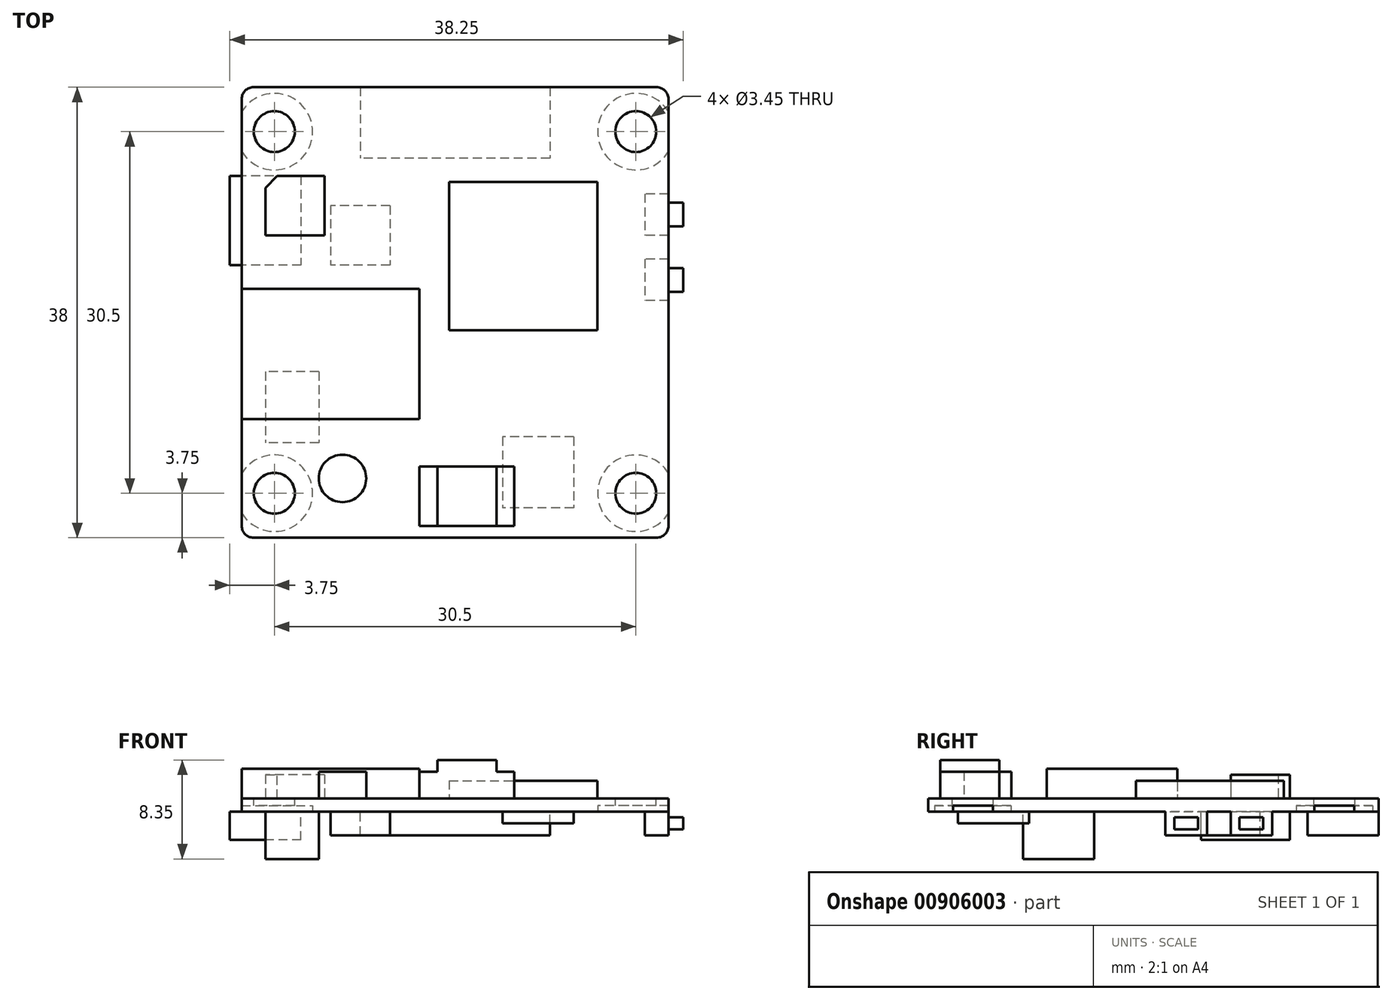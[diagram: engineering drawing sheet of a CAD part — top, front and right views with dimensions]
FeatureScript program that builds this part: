
annotation { "Feature Type Name" : "Feature", "Feature Type Description" : "" }
export const myFeature = defineFeature(function(context is Context, id is Id, definition is map)
    precondition{}
    {
        {
            var Q0;
            Q0=qCreatedBy(makeId("Top.planeOp"),FACE);
            var sketch = newSketch(context, id + "F0", { "sketchPlane" : qUnion([Q0])});
            skLineSegment(sketch, "E0.bottom", {"start": v(17, -19) * mm, "end": v(-17, -19) * mm});
            skLineSegment(sketch, "E0.top", {"start": v(17, 19) * mm, "end": v(-17, 19) * mm});
            skLineSegment(sketch, "E0.left", {"start": v(18, -18) * mm, "end": v(18, 18) * mm});
            skLineSegment(sketch, "E0.right", {"start": v(-18, -18) * mm, "end": v(-18, 18) * mm});
            skPoint(sketch, "E0.middle", {"position": v(0, 0) * mm});
            skPoint(sketch, "E1.visualSharp", {"position": v(-18, 19) * mm});
            skArc(sketch, "E1.filletArc", {"start": v(-17, 19) * mm, "mid": v(-17.7, 18.7) * mm, "end": v(-18, 18) * mm});
            skPoint(sketch, "E2.visualSharp", {"position": v(18, 19) * mm});
            skArc(sketch, "E2.filletArc", {"start": v(18, 18) * mm, "mid": v(17.7, 18.7) * mm, "end": v(17, 19) * mm});
            skPoint(sketch, "E3.visualSharp", {"position": v(-18, -19) * mm});
            skArc(sketch, "E3.filletArc", {"start": v(-18, -18) * mm, "mid": v(-17.7, -18.7) * mm, "end": v(-17, -19) * mm});
            skPoint(sketch, "E4.visualSharp", {"position": v(18, -19) * mm});
            skArc(sketch, "E4.filletArc", {"start": v(17, -19) * mm, "mid": v(17.7, -18.7) * mm, "end": v(18, -18) * mm});
            skSolve(sketch);
        }
        {
            var Q0;
            Q0=qSketchRegion(id+"F0",true);
            extrude(context, id + "F1", {"entities" : qUnion([Q0]), "depth" : 1.1 * mm, "offsetDistance" : 25 * mm});
        }
        {
            var Q0;
            Q0=makeQuery(id+"F1.opExtrude","CAP_FACE",FACE,{"disambiguationData":[OSD([sQuery(id+"F0.wireOp",EDGE,"E0.bottom"),sQuery(id+"F0.wireOp",EDGE,"E0.top"),sQuery(id+"F0.wireOp",EDGE,"E0.left"),sQuery(id+"F0.wireOp",EDGE,"E0.right"),sQuery(id+"F0.wireOp",EDGE,"E1.filletArc"),sQuery(id+"F0.wireOp",EDGE,"E2.filletArc"),sQuery(id+"F0.wireOp",EDGE,"E3.filletArc"),sQuery(id+"F0.wireOp",EDGE,"E4.filletArc")])],"isStart":false});
            var sketch = newSketch(context, id + "F2", { "sketchPlane" : qUnion([Q0])});
            skCircle(sketch, "E5", {"center": v(-15.25, 15.25) * mm, "radius": 1.73 * mm});
            skCircle(sketch, "E6", {"center": v(15.25, 15.25) * mm, "radius": 1.73 * mm});
            skCircle(sketch, "E7", {"center": v(15.25, -15.25) * mm, "radius": 1.73 * mm});
            skCircle(sketch, "E8", {"center": v(-15.25, -15.25) * mm, "radius": 1.73 * mm});
            skSolve(sketch);
        }
        {
            var Q0;
            Q0=qSketchRegion(id+"F2",true);
            extrude(context, id + "F3", {"entities" : qUnion([Q0]), "operationType" : NewBodyOperationType.REMOVE, "endBound" : BoundingType.THROUGH_ALL, "oppositeDirection" : true, "depth" : 25 * mm, "offsetDistance" : 25 * mm});
        }
        {
            var Q0;
            Q0=makeQuery(id+"F1.opExtrude","CAP_FACE",FACE,{"disambiguationData":[OSD([sQuery(id+"F0.wireOp",EDGE,"E0.bottom"),sQuery(id+"F0.wireOp",EDGE,"E0.top"),sQuery(id+"F0.wireOp",EDGE,"E0.left"),sQuery(id+"F0.wireOp",EDGE,"E0.right"),sQuery(id+"F0.wireOp",EDGE,"E1.filletArc"),sQuery(id+"F0.wireOp",EDGE,"E2.filletArc"),sQuery(id+"F0.wireOp",EDGE,"E3.filletArc"),sQuery(id+"F0.wireOp",EDGE,"E4.filletArc")])],"isStart":true});
            var sketch = newSketch(context, id + "F4", { "sketchPlane" : qUnion([Q0])});
            skLineSegment(sketch, "E9.bottom", {"start": v(8, -19) * mm, "end": v(-8, -19) * mm});
            skLineSegment(sketch, "E9.top", {"start": v(8, -13) * mm, "end": v(-8, -13) * mm});
            skLineSegment(sketch, "E9.left", {"start": v(8, -19) * mm, "end": v(8, -13) * mm});
            skLineSegment(sketch, "E9.right", {"start": v(-8, -19) * mm, "end": v(-8, -13) * mm});
            skPoint(sketch, "E10", {"position": v(0, -19) * mm});
            skSolve(sketch);
        }
        {
            var Q0;
            Q0=qSketchRegion(id+"F4",true);
            extrude(context, id + "F5", {"entities" : qUnion([Q0]), "operationType" : NewBodyOperationType.ADD, "depth" : 2 * mm, "offsetDistance" : 25 * mm});
        }
        {
            var Q0;
            Q0=makeQuery(id+"F1.opExtrude","CAP_FACE",FACE,{"disambiguationData":[OSD([sQuery(id+"F0.wireOp",EDGE,"E0.bottom"),sQuery(id+"F0.wireOp",EDGE,"E0.top"),sQuery(id+"F0.wireOp",EDGE,"E0.left"),sQuery(id+"F0.wireOp",EDGE,"E0.right"),sQuery(id+"F0.wireOp",EDGE,"E1.filletArc"),sQuery(id+"F0.wireOp",EDGE,"E2.filletArc"),sQuery(id+"F0.wireOp",EDGE,"E3.filletArc"),sQuery(id+"F0.wireOp",EDGE,"E4.filletArc")])],"isStart":true});
            var sketch = newSketch(context, id + "F6", { "sketchPlane" : qUnion([Q0])});
            skLineSegment(sketch, "E11.bottom", {"start": v(-5.5, -9) * mm, "end": v(-10.5, -9) * mm});
            skLineSegment(sketch, "E11.top", {"start": v(-5.5, -4) * mm, "end": v(-10.5, -4) * mm});
            skLineSegment(sketch, "E11.left", {"start": v(-5.5, -9) * mm, "end": v(-5.5, -4) * mm});
            skLineSegment(sketch, "E11.right", {"start": v(-10.5, -9) * mm, "end": v(-10.5, -4) * mm});
            skPoint(sketch, "E12", {"position": v(-8, -9) * mm});
            skSolve(sketch);
        }
        {
            var Q0;
            Q0=qSketchRegion(id+"F6",true);
            extrude(context, id + "F7", {"entities" : qUnion([Q0]), "operationType" : NewBodyOperationType.ADD, "depth" : 2 * mm, "offsetDistance" : 25 * mm});
        }
        {
            var Q0;
            Q0=makeQuery(id+"F1.opExtrude","CAP_FACE",FACE,{"disambiguationData":[OSD([sQuery(id+"F0.wireOp",EDGE,"E0.bottom"),sQuery(id+"F0.wireOp",EDGE,"E0.top"),sQuery(id+"F0.wireOp",EDGE,"E0.left"),sQuery(id+"F0.wireOp",EDGE,"E0.right"),sQuery(id+"F0.wireOp",EDGE,"E1.filletArc"),sQuery(id+"F0.wireOp",EDGE,"E2.filletArc"),sQuery(id+"F0.wireOp",EDGE,"E3.filletArc"),sQuery(id+"F0.wireOp",EDGE,"E4.filletArc")])],"isStart":true});
            var sketch = newSketch(context, id + "F8", { "sketchPlane" : qUnion([Q0])});
            skLineSegment(sketch, "E13.bottom", {"start": v(-13, -11.5) * mm, "end": v(-19, -11.5) * mm});
            skLineSegment(sketch, "E13.top", {"start": v(-13, -4) * mm, "end": v(-19, -4) * mm});
            skLineSegment(sketch, "E13.left", {"start": v(-13, -11.5) * mm, "end": v(-13, -4) * mm});
            skLineSegment(sketch, "E13.right", {"start": v(-19, -11.5) * mm, "end": v(-19, -4) * mm});
            skSolve(sketch);
        }
        {
            var Q0;
            Q0=qSketchRegion(id+"F8",true);
            extrude(context, id + "F9", {"entities" : qUnion([Q0]), "operationType" : NewBodyOperationType.ADD, "depth" : 2.4 * mm, "offsetDistance" : 25 * mm});
        }
        {
            var Q0;
            Q0=makeQuery(id+"F1.opExtrude","CAP_FACE",FACE,{"disambiguationData":[OSD([sQuery(id+"F0.wireOp",EDGE,"E0.bottom"),sQuery(id+"F0.wireOp",EDGE,"E0.top"),sQuery(id+"F0.wireOp",EDGE,"E0.left"),sQuery(id+"F0.wireOp",EDGE,"E0.right"),sQuery(id+"F0.wireOp",EDGE,"E1.filletArc"),sQuery(id+"F0.wireOp",EDGE,"E2.filletArc"),sQuery(id+"F0.wireOp",EDGE,"E3.filletArc"),sQuery(id+"F0.wireOp",EDGE,"E4.filletArc")])],"isStart":true});
            var sketch = newSketch(context, id + "F10", { "sketchPlane" : qUnion([Q0])});
            skLineSegment(sketch, "E14.bottom", {"start": v(-11.5, 5) * mm, "end": v(-16, 5) * mm});
            skLineSegment(sketch, "E14.top", {"start": v(-11.5, 11) * mm, "end": v(-16, 11) * mm});
            skLineSegment(sketch, "E14.left", {"start": v(-11.5, 5) * mm, "end": v(-11.5, 11) * mm});
            skLineSegment(sketch, "E14.right", {"start": v(-16, 5) * mm, "end": v(-16, 11) * mm});
            skSolve(sketch);
        }
        {
            var Q0;
            Q0=makeQuery(id+"F10.imprint","IMPRINT",FACE,{"disambiguationData":[TD([[makeQuery(id+"F10.imprint","IMPRINT",EDGE,{"derivedFrom":sQuery(id+"F10.wireOp",EDGE,"E14.bottom")}),1.0]])]});
            var sketch = newSketch(context, id + "F11", { "sketchPlane" : qUnion([Q0])});
            skCircle(sketch, "E15.0", {"center": v(15.25, -15.25) * mm, "radius": 1.73 * mm});
            skCircle(sketch, "E16.0", {"center": v(15.25, -15.25) * mm, "radius": 3.23 * mm});
            skCircle(sketch, "E17.0", {"center": v(-15.25, -15.25) * mm, "radius": 3.23 * mm});
            skCircle(sketch, "E18.0", {"center": v(15.25, 15.25) * mm, "radius": 3.23 * mm});
            skCircle(sketch, "E19.0", {"center": v(-15.25, 15.25) * mm, "radius": 3.23 * mm});
            skCircle(sketch, "E20.0", {"center": v(-15.25, -15.25) * mm, "radius": 1.73 * mm});
            skCircle(sketch, "E21.0", {"center": v(-15.25, 15.25) * mm, "radius": 1.73 * mm});
            skCircle(sketch, "E22.0", {"center": v(15.25, 15.25) * mm, "radius": 1.73 * mm});
            skSolve(sketch);
        }
        {
            var Q0;
            Q0=qSketchRegion(id+"F11",true);
            extrude(context, id + "F12", {"entities" : qUnion([Q0]), "operationType" : NewBodyOperationType.REMOVE, "oppositeDirection" : true, "depth" : .5 * mm, "offsetDistance" : 25 * mm});
        }
        {
            var Q0;
            Q0=qSketchRegion(id+"F10",true);
            extrude(context, id + "F13", {"entities" : qUnion([Q0]), "operationType" : NewBodyOperationType.ADD, "depth" : 4 * mm, "offsetDistance" : 25 * mm});
        }
        {
            var Q0;
            Q0=makeQuery(id+"F1.opExtrude","CAP_FACE",FACE,{"disambiguationData":[OSD([sQuery(id+"F0.wireOp",EDGE,"E0.bottom"),sQuery(id+"F0.wireOp",EDGE,"E0.top"),sQuery(id+"F0.wireOp",EDGE,"E0.left"),sQuery(id+"F0.wireOp",EDGE,"E0.right"),sQuery(id+"F0.wireOp",EDGE,"E1.filletArc"),sQuery(id+"F0.wireOp",EDGE,"E2.filletArc"),sQuery(id+"F0.wireOp",EDGE,"E3.filletArc"),sQuery(id+"F0.wireOp",EDGE,"E4.filletArc")])],"isStart":true});
            var sketch = newSketch(context, id + "F14", { "sketchPlane" : qUnion([Q0])});
            skLineSegment(sketch, "E23.bottom", {"start": v(10, 10.5) * mm, "end": v(4, 10.5) * mm});
            skLineSegment(sketch, "E23.top", {"start": v(10, 16.5) * mm, "end": v(4, 16.5) * mm});
            skLineSegment(sketch, "E23.left", {"start": v(10, 10.5) * mm, "end": v(10, 16.5) * mm});
            skLineSegment(sketch, "E23.right", {"start": v(4, 10.5) * mm, "end": v(4, 16.5) * mm});
            skSolve(sketch);
        }
        {
            var Q0;
            Q0=qSketchRegion(id+"F14",true);
            extrude(context, id + "F15", {"entities" : qUnion([Q0]), "operationType" : NewBodyOperationType.ADD, "depth" : 1 * mm, "offsetDistance" : 25 * mm});
        }
        {
            var Q0;
            Q0=makeQuery(id+"F1.opExtrude","CAP_FACE",FACE,{"disambiguationData":[OSD([sQuery(id+"F0.wireOp",EDGE,"E0.bottom"),sQuery(id+"F0.wireOp",EDGE,"E0.top"),sQuery(id+"F0.wireOp",EDGE,"E0.left"),sQuery(id+"F0.wireOp",EDGE,"E0.right"),sQuery(id+"F0.wireOp",EDGE,"E1.filletArc"),sQuery(id+"F0.wireOp",EDGE,"E2.filletArc"),sQuery(id+"F0.wireOp",EDGE,"E3.filletArc"),sQuery(id+"F0.wireOp",EDGE,"E4.filletArc")])],"isStart":true});
            var sketch = newSketch(context, id + "F16", { "sketchPlane" : qUnion([Q0])});
            skLineSegment(sketch, "E24.bottom", {"start": v(18, -10) * mm, "end": v(16, -10) * mm});
            skLineSegment(sketch, "E24.top", {"start": v(18, -6.5) * mm, "end": v(16, -6.5) * mm});
            skLineSegment(sketch, "E24.left", {"start": v(18, -10) * mm, "end": v(18, -6.5) * mm});
            skLineSegment(sketch, "E24.right", {"start": v(16, -10) * mm, "end": v(16, -6.5) * mm});
            skLineSegment(sketch, "E25.bottom", {"start": v(18, -4.5) * mm, "end": v(16, -4.5) * mm});
            skLineSegment(sketch, "E25.top", {"start": v(18, -1) * mm, "end": v(16, -1) * mm});
            skLineSegment(sketch, "E25.left", {"start": v(18, -4.5) * mm, "end": v(18, -1) * mm});
            skLineSegment(sketch, "E25.right", {"start": v(16, -4.5) * mm, "end": v(16, -1) * mm});
            skSolve(sketch);
        }
        {
            var Q0;
            Q0=qSketchRegion(id+"F16",true);
            extrude(context, id + "F17", {"entities" : qUnion([Q0]), "operationType" : NewBodyOperationType.ADD, "depth" : 2 * mm, "offsetDistance" : 25 * mm});
        }
        {
            var Q0;
            Q0=makeQuery(id+"F17.boolean.opBoolean","MERGE",FACE,{"derivedFrom":[makeQuery(id+"F1.opExtrude","SWEPT_FACE",FACE,{"disambiguationData":[OSD([sQuery(id+"F0.wireOp",EDGE,"E0.left")])]}),makeQuery(id+"F17.opExtrude","SWEPT_FACE",FACE,{"disambiguationData":[OSD([sQuery(id+"F16.wireOp",EDGE,"E24.left")])]}),makeQuery(id+"F17.opExtrude","SWEPT_FACE",FACE,{"disambiguationData":[OSD([sQuery(id+"F16.wireOp",EDGE,"E25.left")])]})]});
            var sketch = newSketch(context, id + "F18", { "sketchPlane" : qUnion([Q0])});
            skLineSegment(sketch, "E26.bottom", {"start": v(9.25, -1.5) * mm, "end": v(7.25, -1.5) * mm});
            skLineSegment(sketch, "E26.top", {"start": v(9.25, -0.5) * mm, "end": v(7.25, -0.5) * mm});
            skLineSegment(sketch, "E26.left", {"start": v(9.25, -1.5) * mm, "end": v(9.25, -0.5) * mm});
            skLineSegment(sketch, "E26.right", {"start": v(7.25, -1.5) * mm, "end": v(7.25, -0.5) * mm});
            skPoint(sketch, "E27", {"position": v(8.25, -1.5) * mm});
            skPoint(sketch, "E28", {"position": v(8.25, -2) * mm});
            skPoint(sketch, "E29", {"position": v(7.25, -1) * mm});
            skPoint(sketch, "E30", {"position": v(6.5, -1) * mm});
            skLineSegment(sketch, "E31.bottom", {"start": v(3.75, -1.5) * mm, "end": v(1.75, -1.5) * mm});
            skLineSegment(sketch, "E31.top", {"start": v(3.75, -0.5) * mm, "end": v(1.75, -0.5) * mm});
            skLineSegment(sketch, "E31.left", {"start": v(3.75, -1.5) * mm, "end": v(3.75, -0.5) * mm});
            skLineSegment(sketch, "E31.right", {"start": v(1.75, -1.5) * mm, "end": v(1.75, -0.5) * mm});
            skPoint(sketch, "E32", {"position": v(3.75, -1) * mm});
            skPoint(sketch, "E33", {"position": v(2.75, -2) * mm});
            skPoint(sketch, "E34", {"position": v(2.75, -1.5) * mm});
            skSolve(sketch);
        }
        {
            var Q0;
            Q0=qSketchRegion(id+"F18",true);
            extrude(context, id + "F19", {"entities" : qUnion([Q0]), "operationType" : NewBodyOperationType.ADD, "depth" : 1.25 * mm, "offsetDistance" : 25 * mm});
        }
        {
            var Q0;
            Q0=makeQuery(id+"F1.opExtrude","CAP_FACE",FACE,{"disambiguationData":[OSD([sQuery(id+"F0.wireOp",EDGE,"E0.bottom"),sQuery(id+"F0.wireOp",EDGE,"E0.top"),sQuery(id+"F0.wireOp",EDGE,"E0.left"),sQuery(id+"F0.wireOp",EDGE,"E0.right"),sQuery(id+"F0.wireOp",EDGE,"E1.filletArc"),sQuery(id+"F0.wireOp",EDGE,"E2.filletArc"),sQuery(id+"F0.wireOp",EDGE,"E3.filletArc"),sQuery(id+"F0.wireOp",EDGE,"E4.filletArc")])],"isStart":false});
            var sketch = newSketch(context, id + "F20", { "sketchPlane" : qUnion([Q0])});
            skLineSegment(sketch, "E35.bottom", {"start": v(-0.5, 11) * mm, "end": v(12, 11) * mm});
            skLineSegment(sketch, "E35.top", {"start": v(-0.5, -1.5) * mm, "end": v(12, -1.5) * mm});
            skLineSegment(sketch, "E35.left", {"start": v(-0.5, 11) * mm, "end": v(-0.5, -1.5) * mm});
            skLineSegment(sketch, "E35.right", {"start": v(12, 11) * mm, "end": v(12, -1.5) * mm});
            skSolve(sketch);
        }
        {
            var Q0;
            Q0=qSketchRegion(id+"F20",true);
            extrude(context, id + "F21", {"entities" : qUnion([Q0]), "operationType" : NewBodyOperationType.ADD, "depth" : 1.5 * mm, "offsetDistance" : 25 * mm});
        }
        {
            var Q0;
            Q0=makeQuery(id+"F1.opExtrude","CAP_FACE",FACE,{"disambiguationData":[OSD([sQuery(id+"F0.wireOp",EDGE,"E0.bottom"),sQuery(id+"F0.wireOp",EDGE,"E0.top"),sQuery(id+"F0.wireOp",EDGE,"E0.left"),sQuery(id+"F0.wireOp",EDGE,"E0.right"),sQuery(id+"F0.wireOp",EDGE,"E1.filletArc"),sQuery(id+"F0.wireOp",EDGE,"E2.filletArc"),sQuery(id+"F0.wireOp",EDGE,"E3.filletArc"),sQuery(id+"F0.wireOp",EDGE,"E4.filletArc")])],"isStart":false});
            var sketch = newSketch(context, id + "F22", { "sketchPlane" : qUnion([Q0])});
            skLineSegment(sketch, "E36.bottom", {"start": v(-3, 2) * mm, "end": v(-18, 2) * mm});
            skLineSegment(sketch, "E36.top", {"start": v(-3, -9) * mm, "end": v(-18, -9) * mm});
            skLineSegment(sketch, "E36.left", {"start": v(-3, 2) * mm, "end": v(-3, -9) * mm});
            skLineSegment(sketch, "E36.right", {"start": v(-18, 2) * mm, "end": v(-18, -9) * mm});
            skSolve(sketch);
        }
        {
            var Q0;
            Q0=qSketchRegion(id+"F22",true);
            extrude(context, id + "F23", {"entities" : qUnion([Q0]), "operationType" : NewBodyOperationType.ADD, "depth" : 2.5 * mm, "offsetDistance" : 25 * mm});
        }
        {
            var Q0;
            Q0=makeQuery(id+"F1.opExtrude","CAP_FACE",FACE,{"disambiguationData":[OSD([sQuery(id+"F0.wireOp",EDGE,"E0.bottom"),sQuery(id+"F0.wireOp",EDGE,"E0.top"),sQuery(id+"F0.wireOp",EDGE,"E0.left"),sQuery(id+"F0.wireOp",EDGE,"E0.right"),sQuery(id+"F0.wireOp",EDGE,"E1.filletArc"),sQuery(id+"F0.wireOp",EDGE,"E2.filletArc"),sQuery(id+"F0.wireOp",EDGE,"E3.filletArc"),sQuery(id+"F0.wireOp",EDGE,"E4.filletArc")])],"isStart":false});
            var sketch = newSketch(context, id + "F24", { "sketchPlane" : qUnion([Q0])});
            skLineSegment(sketch, "E37.bottom", {"start": v(5, -18) * mm, "end": v(-3, -18) * mm});
            skLineSegment(sketch, "E37.top", {"start": v(5, -13) * mm, "end": v(-3, -13) * mm});
            skLineSegment(sketch, "E37.left", {"start": v(5, -18) * mm, "end": v(5, -13) * mm});
            skLineSegment(sketch, "E37.right", {"start": v(-3, -18) * mm, "end": v(-3, -13) * mm});
            skSolve(sketch);
        }
        {
            var Q0;
            Q0=qSketchRegion(id+"F24",true);
            extrude(context, id + "F25", {"entities" : qUnion([Q0]), "operationType" : NewBodyOperationType.ADD, "depth" : 2.25 * mm, "offsetDistance" : 25 * mm});
        }
        {
            var Q0;
            Q0=makeQuery(id+"F25.opExtrude","CAP_FACE",FACE,{"disambiguationData":[OSD([sQuery(id+"F24.wireOp",EDGE,"E37.bottom"),sQuery(id+"F24.wireOp",EDGE,"E37.top"),sQuery(id+"F24.wireOp",EDGE,"E37.left"),sQuery(id+"F24.wireOp",EDGE,"E37.right")])],"isStart":false});
            var sketch = newSketch(context, id + "F26", { "sketchPlane" : qUnion([Q0])});
            skLineSegment(sketch, "E38.bottom", {"start": v(3.5, -13) * mm, "end": v(-1.5, -13) * mm});
            skLineSegment(sketch, "E38.top", {"start": v(3.5, -18) * mm, "end": v(-1.5, -18) * mm});
            skLineSegment(sketch, "E38.left", {"start": v(3.5, -13) * mm, "end": v(3.5, -18) * mm});
            skLineSegment(sketch, "E38.right", {"start": v(-1.5, -13) * mm, "end": v(-1.5, -18) * mm});
            skSolve(sketch);
        }
        {
            var Q0;
            Q0=qSketchRegion(id+"F26",true);
            extrude(context, id + "F27", {"entities" : qUnion([Q0]), "operationType" : NewBodyOperationType.ADD, "depth" : 1 * mm, "offsetDistance" : 25 * mm});
        }
        {
            var Q0;
            Q0=makeQuery(id+"F1.opExtrude","CAP_FACE",FACE,{"disambiguationData":[OSD([sQuery(id+"F0.wireOp",EDGE,"E0.bottom"),sQuery(id+"F0.wireOp",EDGE,"E0.top"),sQuery(id+"F0.wireOp",EDGE,"E0.left"),sQuery(id+"F0.wireOp",EDGE,"E0.right"),sQuery(id+"F0.wireOp",EDGE,"E1.filletArc"),sQuery(id+"F0.wireOp",EDGE,"E2.filletArc"),sQuery(id+"F0.wireOp",EDGE,"E3.filletArc"),sQuery(id+"F0.wireOp",EDGE,"E4.filletArc")])],"isStart":false});
            var sketch = newSketch(context, id + "F28", { "sketchPlane" : qUnion([Q0])});
            skCircle(sketch, "E39", {"center": v(-9.5, -14) * mm, "radius": 2 * mm});
            skSolve(sketch);
        }
        {
            var Q0;
            Q0=qSketchRegion(id+"F28",true);
            extrude(context, id + "F29", {"entities" : qUnion([Q0]), "operationType" : NewBodyOperationType.ADD, "depth" : 2.25 * mm, "offsetDistance" : 25 * mm});
        }
        {
            var Q0;
            Q0=makeQuery(id+"F1.opExtrude","CAP_FACE",FACE,{"disambiguationData":[OSD([sQuery(id+"F0.wireOp",EDGE,"E0.bottom"),sQuery(id+"F0.wireOp",EDGE,"E0.top"),sQuery(id+"F0.wireOp",EDGE,"E0.left"),sQuery(id+"F0.wireOp",EDGE,"E0.right"),sQuery(id+"F0.wireOp",EDGE,"E1.filletArc"),sQuery(id+"F0.wireOp",EDGE,"E2.filletArc"),sQuery(id+"F0.wireOp",EDGE,"E3.filletArc"),sQuery(id+"F0.wireOp",EDGE,"E4.filletArc")])],"isStart":false});
            var sketch = newSketch(context, id + "F30", { "sketchPlane" : qUnion([Q0])});
            skLineSegment(sketch, "E40.bottom", {"start": v(-11, 11.5) * mm, "end": v(-16, 11.5) * mm});
            skLineSegment(sketch, "E40.top", {"start": v(-11, 6.5) * mm, "end": v(-16, 6.5) * mm});
            skLineSegment(sketch, "E40.left", {"start": v(-11, 11.5) * mm, "end": v(-11, 6.5) * mm});
            skLineSegment(sketch, "E40.right", {"start": v(-16, 11.5) * mm, "end": v(-16, 6.5) * mm});
            skSolve(sketch);
        }
        {
            var Q0;
            Q0=qSketchRegion(id+"F30",true);
            extrude(context, id + "F31", {"entities" : qUnion([Q0]), "operationType" : NewBodyOperationType.ADD, "depth" : 2 * mm, "offsetDistance" : 25 * mm});
        }
        {
            var Q0;
            Q0=makeQuery(id+"F31.opExtrude","SWEPT_EDGE",EDGE,{"disambiguationData":[OSD([sQuery(id+"F30.wireOp",EDGE,"E40.bottom"),sQuery(id+"F30.wireOp",EDGE,"E40.right")])]});
            chamfer(context, id + "F32", {"entities" : qUnion([Q0]), "width" : 1 * mm, "tangentPropagation" : true});
        }
    });
